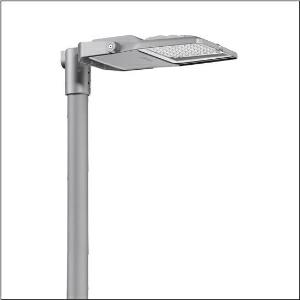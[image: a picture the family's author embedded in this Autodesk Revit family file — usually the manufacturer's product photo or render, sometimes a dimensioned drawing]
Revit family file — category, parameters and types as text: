
# Revit family: floodlight_fl_21_mini___pl64_5xa7775d2e3a_010e
name_source: partatom
category: Lighting Fixtures
units: mm (PartAtom-declared; Revit-internal decimal feet)

## family parameters
Cut with Voids When Loaded = No
Host = Face
Light Source = No
Part Type = Normal
Room Calculation Point = No
Round Connector Dimension = Use Diameter
Shared = No

## types (1)
- --- (1 x LED, 17220 lm, 142.9 W, 3000K)
    Apparent Load = 143 VA
    CIE Flux Codes = 28 80 98 100 100
    Color Rendering = 70
    Color Temperature = 3000K
    Default Elevation = 1800 mm
    Description = Floodlight FL 21 mini, floodlight, primary light control with lens, of PMMA, primary optical cover: protective disc, of toughened safety glass, transparent, light distribution: PL64, light emission: direct distribution, installation type: surface-mounted, LED, High Power LED, rated luminous flux: 17.220lm, luminous efficacy: 121lm/W, light colour: 730, colour temperature: 3000K, control: flexible luminous flux parameterisation, time-dependent luminous flux control, constant luminous flux control, overheat protection, presetting dimming logarithmic, with terminal, 6-pole, mains connection: 220..240V, AC, 50/60Hz, start of lifetime: 143W, end of service life: 151W, reduction: 63W, luminaire housing, of diecast aluminium, powder-coated, Siteco® metallic grey (DB 702S), corrosivity category C5 mid according to DIN EN ISO 12944, sealing non-destructively replaceable, please order mast flange separately, mast bracket, of steel, galvanised, powder-coated, Siteco® metallic grey (DB 702S), Smart Interface above, protection rating (complete): IP66, insulation class (complete): insulation class II (safety insulation), certification: CE, ENEC, VDE, protection symbol: D, impact resistance: IK08, permissible operating ambient temperature: -40..+40°C, permissible operating ambient temperature for outdoor applications: -40..+50°C, standard: DIN EN 12944, LABS conformity tested according to VDMA 24364:2018-05, packaging unit: 1 piece

Light Distribution: PL64
    Height = 70 mm
    Lamp = 1 x LED
    Lamp Light Flux = 17220 lm
    Lamp Power = 142.9 W
    Lamp count = 1
    Length = 485 mm
    Luminous efficacy = 121 lm/W
    Manufacturer = Siteco
    ModVariant = No
    Model = 5XA7775D2E3A
    Number of Poles = 1
    OnlyDefault = Yes
    Power Factor = 1
    Product Name = Floodlight FL 21 mini | PL64
    Product group = floodlight | pylon annexe
    ProductGroupID = 6200
    Protection Class = Protection class II
    Protection Degree = IP 66
    RLX_Detail_Level = 1
    RLX_Emergency_Light_Flux = 0 lm
    RLX_Emergency_Type = 0
    RLX_Emergency_Type_DB = No
    RlxData = <blob elided: 101209 chars, md5=3b374fd8>
    Socket = socket
    Standby Power = 0 W
    System Light Flux = 17220 lm
    System Power = 143 W
    Type Comments = factory setting: luminous flux: 100 % | dim-lin: 254 | 730 mA
    Type Image = l_1007125.jpg
    URL = http://relux.com
    VarID = @adj_097575
    Voltage = 0 V
    Weight = 0.00 kg
    Width = 337 mm

## geometry (parser evidence)
native form markers: Blend x4, Sweep x14
no freeform markers — native parametric forms only
